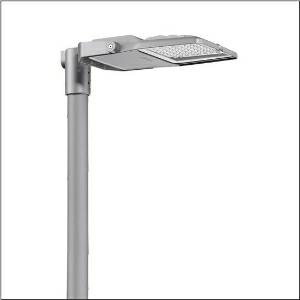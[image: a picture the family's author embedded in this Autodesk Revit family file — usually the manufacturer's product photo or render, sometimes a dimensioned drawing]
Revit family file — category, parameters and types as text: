
# Revit family: floodlight_fl_21_iq_mini___pl43_5xa7771c2a3a_69d2
name_source: partatom
category: Lighting Fixtures
units: mm (PartAtom-declared; Revit-internal decimal feet)

## family parameters
Cut with Voids When Loaded = No
Host = Face
Light Source = No
Part Type = Normal
Room Calculation Point = No
Round Connector Dimension = Use Diameter
Shared = No

## types (1)
- --- (1 x LED, 12520 lm, 87.2 W, 3000K)
    Apparent Load = 87 VA
    CIE Flux Codes = 27 78 99 100 100
    Color Rendering = 70
    Color Temperature = 3000K
    Default Elevation = 1800 mm
    Description = Floodlight FL 21 iQ mini, floodlight, primary light control with lens, of PMMA, primary optical cover: protective disc, of toughened safety glass, transparent, light distribution: PL43, light emission: direct distribution, installation type: surface-mounted, LED, High Power LED, rated luminous flux: 12.520lm, luminous efficacy: 144lm/W, light colour: 730, colour temperature: 3000K, control gear: iQ Comfort/DALI, control: Auto-Match, Temp-Guard, Lumen-Switch, Night-Set, Smart-Wire, Light-Fading, Desk-Remote (wireless, voltage-free reading and setting of iQ features in the workshop via application-optimized NFC function/RFID function), optimised constant luminous flux control (CLO 2.0), with terminal, 6-pole, mains connection: 220..240V, AC, 50/60Hz, start of lifetime: 87W, end of service life: 92W, reduction: 40W, luminaire housing, of diecast aluminium, powder-coated, Siteco® metallic grey (DB 702S), corrosivity category C5 mid according to DIN EN ISO 12944, suitable for swimming pools, chlorine-resistant, sealing non-destructively replaceable, please order mast flange separately, mast bracket, of steel, galvanised, powder-coated, Siteco® metallic grey (DB 702S), protection rating (complete): IP66, insulation class (complete): insulation class II (safety insulation), certification: CE, ENEC, VDE, protection symbol: D, impact resistance: IK08, permissible operating ambient temperature: -40..+40°C, permissible operating ambient temperature for outdoor applications: -40..+50°C, standard: DIN EN 12944, LABS conformity tested according to VDMA 24364:2018-05, packaging unit: 1 piece

Light Distribution: PL43
    Height = 70 mm
    Lamp = 1 x LED
    Lamp Light Flux = 12520 lm
    Lamp Power = 87.2 W
    Lamp count = 1
    Length = 485 mm
    Luminous efficacy = 144 lm/W
    Manufacturer = Siteco
    ModVariant = No
    Model = 5XA7771C2A3A
    Number of Poles = 1
    OnlyDefault = Yes
    Power Factor = 1
    Product Name = Floodlight FL 21 iQ mini | PL43
    Product group = floodlight | pylon annexe
    ProductGroupID = 6200
    Protection Class = Protection class II
    Protection Degree = IP 66
    RLX_Detail_Level = 1
    RLX_Emergency_Light_Flux = 0 lm
    RLX_Emergency_Type = 0
    RLX_Emergency_Type_DB = No
    RlxData = <blob elided: 101341 chars, md5=f014a67f>
    Socket = socket
    Standby Power = 0 W
    System Light Flux = 12520 lm
    System Power = 87 W
    Type Comments = factory setting: luminous flux: 100 % | dim-lin: 254 | 456 mA
    Type Image = l_1007125.jpg
    URL = http://relux.com
    VarID = @adj_162502
    Voltage = 0 V
    Weight = 0.00 kg
    Width = 337 mm

## geometry (parser evidence)
native form markers: Blend x4, Sweep x13
no freeform markers — native parametric forms only
